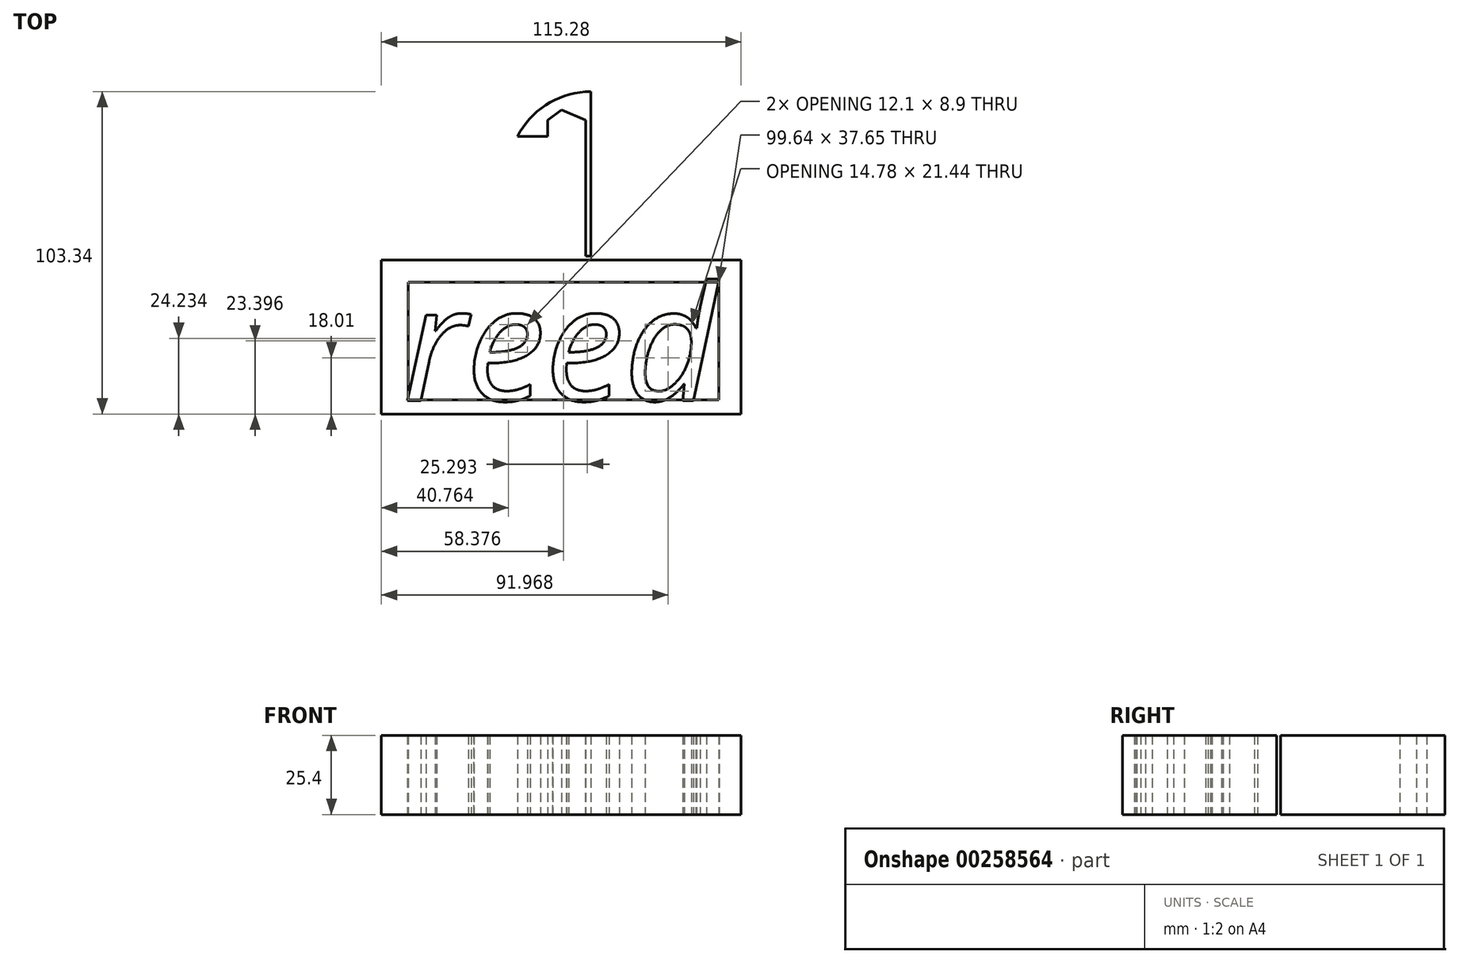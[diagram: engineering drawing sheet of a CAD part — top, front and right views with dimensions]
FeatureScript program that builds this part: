
annotation { "Feature Type Name" : "Feature", "Feature Type Description" : "" }
export const myFeature = defineFeature(function(context is Context, id is Id, definition is map)
    precondition{}
    {
        {
            var Q0;
            Q0=qCreatedBy(makeId("Top.planeOp"),FACE);
            var sketch = newSketch(context, id + "F0", { "sketchPlane" : qUnion([Q0])});
            skText(sketch, "E0", { "text": "reed", "fontName": "OpenSans-Italic.ttf"});
            skLineSegment(sketch, "E1.bottom", {"start": v(-8.3, -39) * mm, "end": v(6.22, -39) * mm, "construction": true});
            skLineSegment(sketch, "E1.top", {"start": v(-8.3, 0) * mm, "end": v(6.22, 0) * mm, "construction": true});
            skLineSegment(sketch, "E1.left", {"start": v(-8.3, -39) * mm, "end": v(-8.3, 0) * mm, "construction": true});
            skLineSegment(sketch, "E1.right", {"start": v(6.22, -39) * mm, "end": v(6.22, 0) * mm, "construction": true});
            skLineSegment(sketch, "E2", {"start": v(-8.3, 0) * mm, "end": v(-31.53, 15.35) * mm});
            skLineSegment(sketch, "E3", {"start": v(-31.53, 15.35) * mm, "end": v(24.08, 15.35) * mm});
            skLineSegment(sketch, "E4", {"start": v(24.08, 15.35) * mm, "end": v(6.22, 0) * mm});
            skPoint(sketch, "E5", {"position": v(-3.73, 22.3) * mm});
            skPoint(sketch, "E5.positionSnap0", {"position": v(-3.73, 15.35) * mm});
            const initialGuessF0  = {"E0": [-0.05394, -0.07593, 1, 0, 0.03693]};
            skSetInitialGuess(sketch, initialGuessF0);
            skSolve(sketch);
        }
        {
            var Q0;
            Q0 = qSketchRegion(id + "F0", true);
            extrude(context, id + "F1", {"entities" : qUnion([Q0]), "depth" : 25.4 * mm});
        }
        {
            var Q0;
            Q0=qCreatedBy(makeId("Top.planeOp"),FACE);
            var sketch = newSketch(context, id + "F2", { "sketchPlane" : qUnion([Q0])});
            skLineSegment(sketch, "E6.bottom", {"start": v(-52.3, -75.67) * mm, "end": v(41.1, -75.67) * mm});
            skLineSegment(sketch, "E6.top", {"start": v(-52.3, -80.24) * mm, "end": v(41.1, -80.24) * mm});
            skLineSegment(sketch, "E6.left", {"start": v(-52.3, -75.67) * mm, "end": v(-52.3, -80.24) * mm});
            skLineSegment(sketch, "E6.right", {"start": v(41.1, -75.67) * mm, "end": v(41.1, -80.24) * mm});
            skPoint(sketch, "E7.oppositeSnap0", {"position": v(-5.6, -80.24) * mm});
            skLineSegment(sketch, "E7.bottom", {"start": v(-52.3, -75.67) * mm, "end": v(47.34, -75.67) * mm});
            skLineSegment(sketch, "E7.top", {"start": v(-52.3, -80.24) * mm, "end": v(47.34, -80.24) * mm});
            skLineSegment(sketch, "E7.right", {"start": v(47.34, -75.67) * mm, "end": v(47.34, -80.24) * mm});
            skLineSegment(sketch, "E8.bottom", {"start": v(47.34, -75.67) * mm, "end": v(47.34, -75.67) * mm});
            skLineSegment(sketch, "E8.top", {"start": v(47.34, -80.24) * mm, "end": v(47.34, -80.24) * mm});
            skLineSegment(sketch, "E9.bottom", {"start": v(47.34, -80.24) * mm, "end": v(54.42, -80.24) * mm});
            skLineSegment(sketch, "E9.top", {"start": v(47.34, -30.9) * mm, "end": v(54.42, -30.9) * mm});
            skLineSegment(sketch, "E9.left", {"start": v(47.34, -80.24) * mm, "end": v(47.34, -30.9) * mm});
            skLineSegment(sketch, "E9.right", {"start": v(54.42, -80.24) * mm, "end": v(54.42, -30.9) * mm});
            skLineSegment(sketch, "E10.bottom", {"start": v(54.42, -30.9) * mm, "end": v(-54, -30.9) * mm});
            skLineSegment(sketch, "E10.top", {"start": v(54.42, -38.02) * mm, "end": v(-54, -38.02) * mm});
            skLineSegment(sketch, "E10.left", {"start": v(54.42, -30.9) * mm, "end": v(54.42, -38.02) * mm});
            skLineSegment(sketch, "E10.right", {"start": v(-54, -30.9) * mm, "end": v(-54, -38.02) * mm});
            skLineSegment(sketch, "E11.bottom", {"start": v(-52.3, -80.24) * mm, "end": v(-54, -80.24) * mm});
            skLineSegment(sketch, "E11.top", {"start": v(-52.3, -30.9) * mm, "end": v(-54, -30.9) * mm});
            skLineSegment(sketch, "E11.left", {"start": v(-52.3, -80.24) * mm, "end": v(-52.3, -30.9) * mm});
            skLineSegment(sketch, "E11.right", {"start": v(-54, -80.24) * mm, "end": v(-54, -30.9) * mm});
            skLineSegment(sketch, "E12.bottom", {"start": v(-52.3, -80.24) * mm, "end": v(-60.86, -80.24) * mm});
            skLineSegment(sketch, "E12.top", {"start": v(-52.3, -30.9) * mm, "end": v(-60.86, -30.9) * mm});
            skLineSegment(sketch, "E12.right", {"start": v(-60.86, -80.24) * mm, "end": v(-60.86, -30.9) * mm});
            skSolve(sketch);
        }
        {
            var Q0;
            Q0 = qSketchRegion(id + "F2", true);
            extrude(context, id + "F3", {"entities" : qUnion([Q0]), "depth" : 25.4 * mm});
        }
        {
            var Q0;
            Q0=qCreatedBy(makeId("Top.planeOp"),FACE);
            var sketch = newSketch(context, id + "F4", { "sketchPlane" : qUnion([Q0])});
            skLineSegment(sketch, "E13.bottom", {"start": v(6.28, -29.65) * mm, "end": v(4.6, -29.65) * mm});
            skLineSegment(sketch, "E13.top", {"start": v(6.28, 23.1) * mm, "end": v(4.6, 23.1) * mm});
            skLineSegment(sketch, "E13.left", {"start": v(6.28, -29.65) * mm, "end": v(6.28, 23.1) * mm});
            skLineSegment(sketch, "E13.right", {"start": v(4.6, -29.65) * mm, "end": v(4.6, 23.1) * mm});
            skArc(sketch, "E14", {"start": v(6.28, 23.1) * mm, "mid": v(-7.5, 19.2) * mm, "end": v(-17.23, 8.68) * mm});
            skLineSegment(sketch, "E15", {"start": v(-17.23, 8.68) * mm, "end": v(-7.5, 8.68) * mm});
            skPoint(sketch, "E15.endSnap0", {"position": v(-7.5, 19.2) * mm});
            skLineSegment(sketch, "E16", {"start": v(-7.5, 8.68) * mm, "end": v(-7.5, 19.2) * mm});
            skLineSegment(sketch, "E17", {"start": v(4.6, 13.94) * mm, "end": v(-7.5, 19.2) * mm});
            skPoint(sketch, "E17.startSnap0", {"position": v(-7.5, 13.94) * mm});
            skLineSegment(sketch, "E18", {"start": v(4.6, 23.1) * mm, "end": v(-7.5, 13.94) * mm});
            skSolve(sketch);
        }
        {
            var Q0;
            Q0 = qSketchRegion(id + "F4", true);
            extrude(context, id + "F5", {"entities" : qUnion([Q0]), "depth" : 25.4 * mm});
        }
    });
